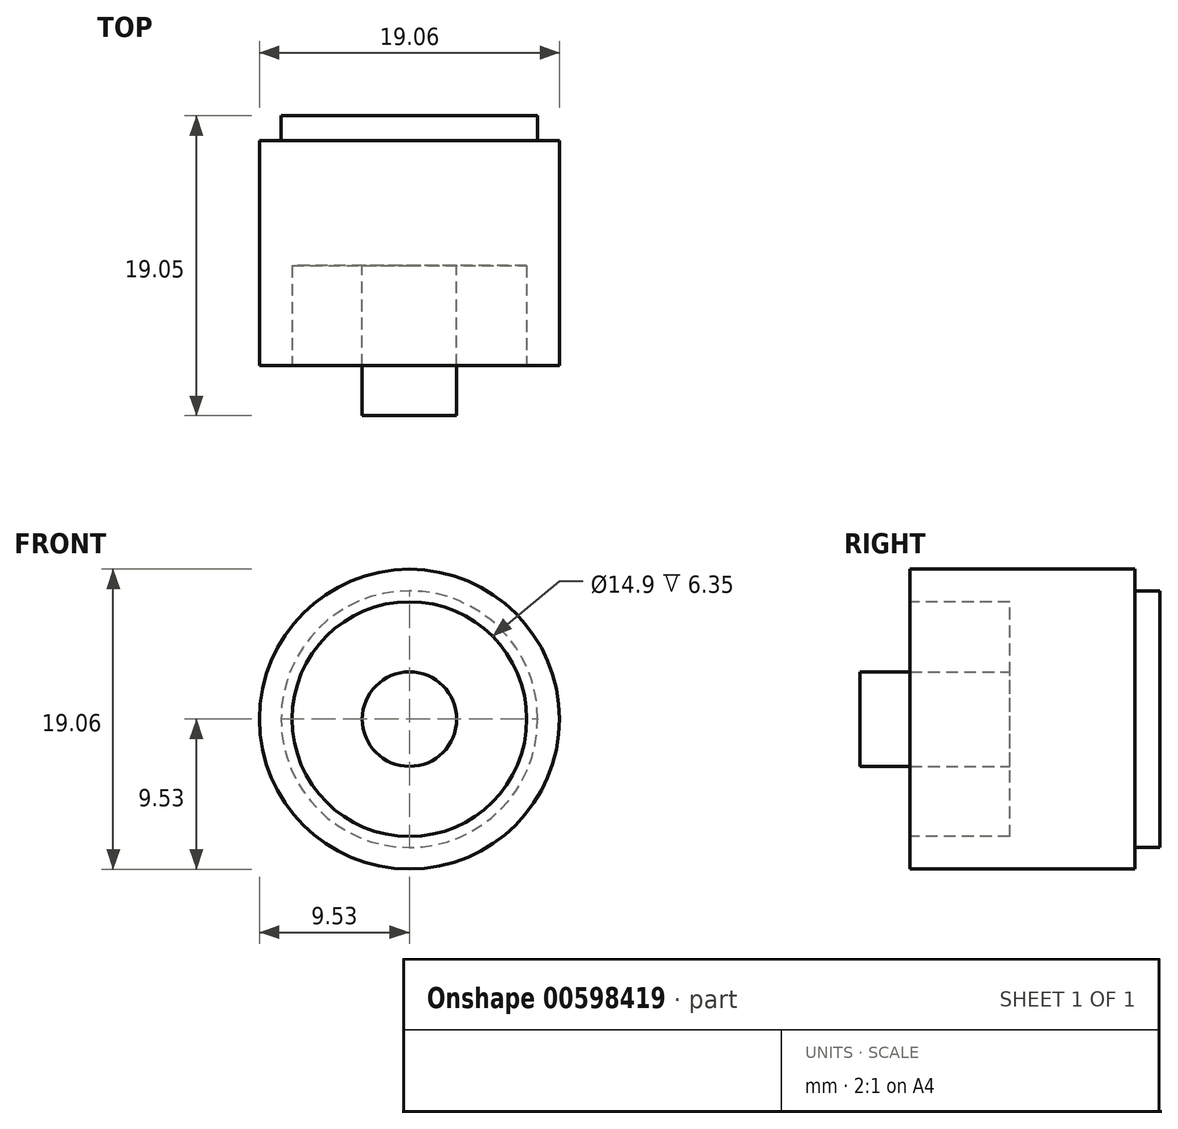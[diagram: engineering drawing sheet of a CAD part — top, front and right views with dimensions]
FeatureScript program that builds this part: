
annotation { "Feature Type Name" : "Feature", "Feature Type Description" : "" }
export const myFeature = defineFeature(function(context is Context, id is Id, definition is map)
    precondition{}
    {
        {
            var Q0;
            Q0=qCreatedBy(makeId("Front.planeOp"),FACE);
            var sketch = newSketch(context, id + "F0", { "sketchPlane" : qUnion([Q0])});
            skCircle(sketch, "E0", {"center": v(0, 0) * mm, "radius": 9.53 * mm});
            skSolve(sketch);
        }
        {
            var Q0;
            Q0 = qSketchRegion(id + "F0", true);
            extrude(context, id + "F1", {"entities" : qUnion([Q0]), "depth" : 14.29 * mm, "offsetDistance" : 25.4 * mm});
        }
        {
            var Q0;
            Q0=makeQuery(id+"F1.opExtrude","CAP_FACE",FACE,{"disambiguationData":[OSD([sQuery(id+"F0.wireOp",EDGE,"E0")])],"isStart":true});
            var sketch = newSketch(context, id + "F2", { "sketchPlane" : qUnion([Q0])});
            skCircle(sketch, "E1", {"center": v(0, 0) * mm, "radius": 8.15 * mm});
            skSolve(sketch);
        }
        {
            var Q0;
            Q0 = qSketchRegion(id + "F2", true);
            extrude(context, id + "F3", {"entities" : qUnion([Q0]), "operationType" : NewBodyOperationType.ADD, "depth" : 1.59 * mm, "offsetDistance" : 25.4 * mm});
        }
        {
            var Q0;
            Q0=makeQuery(id+"F1.opExtrude","CAP_FACE",FACE,{"disambiguationData":[OSD([sQuery(id+"F0.wireOp",EDGE,"E0")])],"isStart":false});
            var sketch = newSketch(context, id + "F4", { "sketchPlane" : qUnion([Q0])});
            skCircle(sketch, "E2", {"center": v(0, 0) * mm, "radius": 7.45 * mm});
            skSolve(sketch);
        }
        {
            var Q0;
            Q0 = qSketchRegion(id + "F4", true);
            extrude(context, id + "F5", {"entities" : qUnion([Q0]), "operationType" : NewBodyOperationType.REMOVE, "oppositeDirection" : true, "depth" : 6.35 * mm, "offsetDistance" : 25.4 * mm});
        }
        {
            var Q0;
            Q0=makeQuery(id+"F5.boolean.opBoolean","COPY",FACE,{"derivedFrom":makeQuery(id+"F5.opExtrude","CAP_FACE",FACE,{"disambiguationData":[OSD([sQuery(id+"F4.wireOp",EDGE,"E2")])],"isStart":false})});
            var sketch = newSketch(context, id + "F6", { "sketchPlane" : qUnion([Q0])});
            skCircle(sketch, "E3", {"center": v(0, 0) * mm, "radius": 3 * mm});
            skSolve(sketch);
        }
        {
            var Q0;
            Q0=makeQuery(id+"F6.imprint","IMPRINT",FACE,{"disambiguationData":[TD([[makeQuery(id+"F6.imprint","IMPRINT",EDGE,{"derivedFrom":sQuery(id+"F6.wireOp",EDGE,"E3")}),1.0]])]});
            extrude(context, id + "F7", {"entities" : qUnion([Q0]), "operationType" : NewBodyOperationType.ADD, "depth" : 9.52 * mm, "offsetDistance" : 25.4 * mm});
        }
    });
